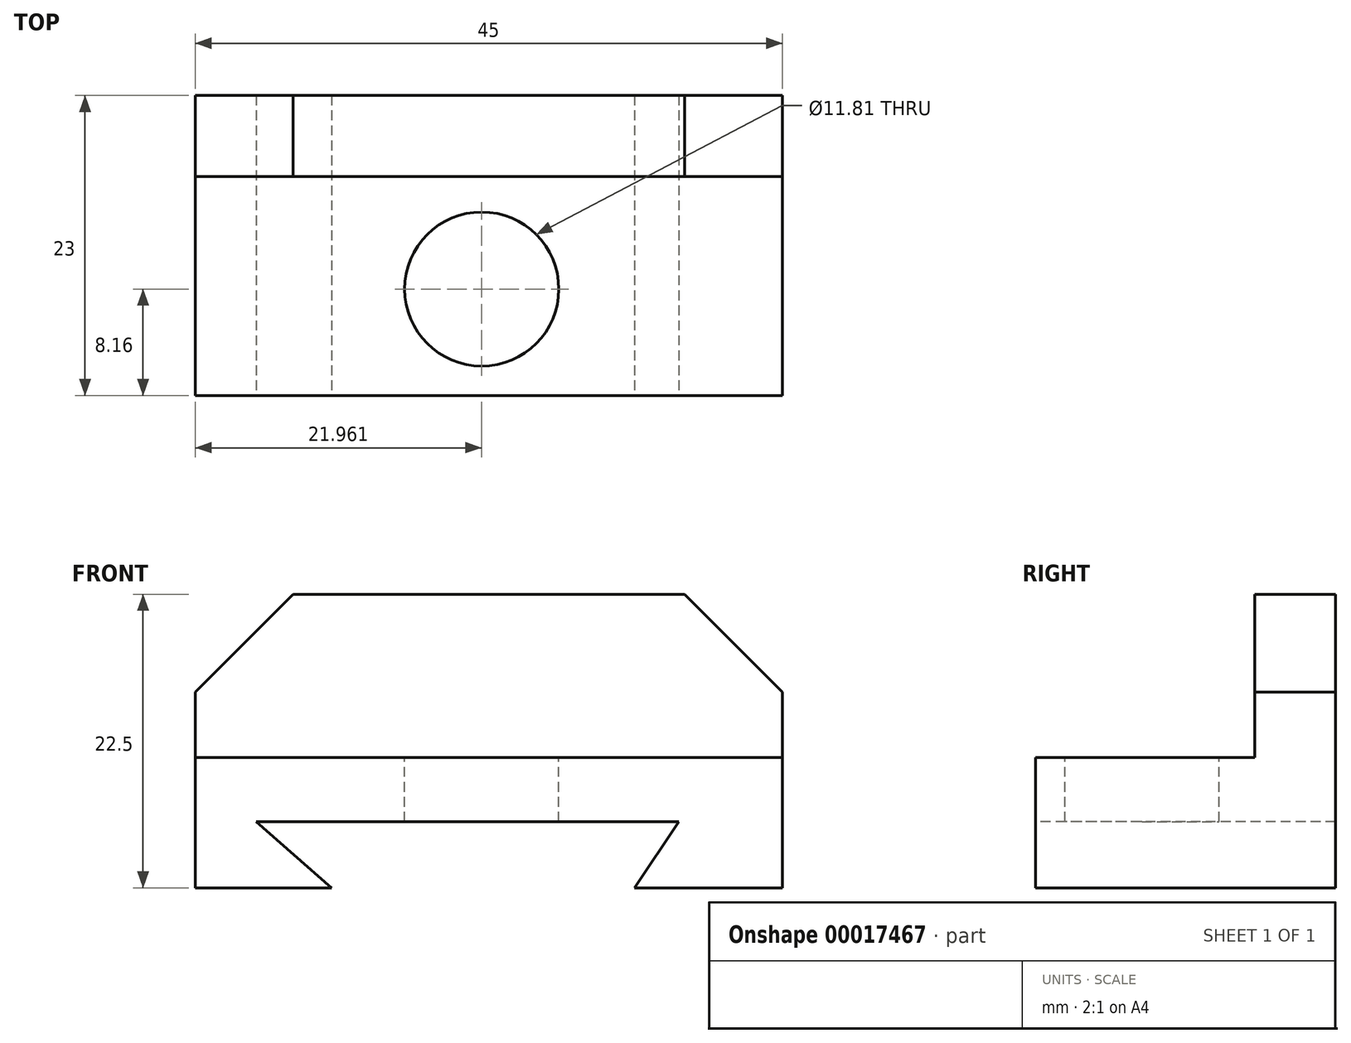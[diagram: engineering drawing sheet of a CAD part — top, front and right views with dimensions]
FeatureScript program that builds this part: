
annotation { "Feature Type Name" : "Feature", "Feature Type Description" : "" }
export const myFeature = defineFeature(function(context is Context, id is Id, definition is map)
    precondition{}
    {
        {
            var Q0;
            Q0=qCreatedBy(makeId("Front.planeOp"),FACE);
            var sketch = newSketch(context, id + "F0", { "sketchPlane" : qUnion([Q0])});
            skLineSegment(sketch, "E0", {"start": v(0, 0) * mm, "end": v(0, 15) * mm});
            skLineSegment(sketch, "E1", {"start": v(0, 15) * mm, "end": v(-7.5, 22.5) * mm});
            skLineSegment(sketch, "E2", {"start": v(-7.5, 22.5) * mm, "end": v(-37.5, 22.5) * mm});
            skLineSegment(sketch, "E3", {"start": v(-37.5, 22.5) * mm, "end": v(-45, 15) * mm});
            skLineSegment(sketch, "E4", {"start": v(-45, 15) * mm, "end": v(-45, 0) * mm});
            skLineSegment(sketch, "E5", {"start": v(-45, 0) * mm, "end": v(0, 0) * mm});
            skLineSegment(sketch, "E6", {"start": v(-45, 15) * mm, "end": v(-45, 10) * mm});
            skLineSegment(sketch, "E7", {"start": v(-45, 10) * mm, "end": v(0, 10) * mm});
            skSolve(sketch);
        }
        {
            var Q0;
            {var subQ1=sQuery(id+"F0.wireOp",EDGE,"E1");Q0=makeQuery(id+"F0.imprint","IMPRINT",FACE,{"disambiguationData":[TD([[makeQuery(id+"F0.imprint","IMPRINT",EDGE,{"derivedFrom":subQ1}),1.0]])]});}
            var Q1;
            Q1=makeQuery(id+"F0.imprint","IMPRINT",FACE,{"disambiguationData":[TD([[makeQuery(id+"F0.imprint","IMPRINT",EDGE,{"derivedFrom":sQuery(id+"F0.wireOp",EDGE,"E4")}),1.0]])]});
            extrude(context, id + "F1", {"entities" : qUnion([Q0, Q1]), "oppositeDirection" : true, "depth" : 6.2 * mm});
        }
        {
            var Q0;
            Q0=makeQuery(id+"F0.imprint","IMPRINT",FACE,{"disambiguationData":[TD([[makeQuery(id+"F0.imprint","IMPRINT",EDGE,{"derivedFrom":sQuery(id+"F0.wireOp",EDGE,"E4")}),1.0]])]});
            extrude(context, id + "F2", {"entities" : qUnion([Q0]), "operationType" : NewBodyOperationType.ADD, "depth" : 16.8 * mm});
        }
        {
            var Q0;
            Q0=makeQuery(id+"F2.opExtrude","SWEPT_FACE",FACE,{"disambiguationData":[OSD([sQuery(id+"F0.wireOp",EDGE,"E7")])]});
            var sketch = newSketch(context, id + "F3", { "sketchPlane" : qUnion([Q0])});
            skCircle(sketch, "E8", {"center": v(-23.04, -8.64) * mm, "radius": 5.9 * mm});
            skSolve(sketch);
        }
        {
            var Q0;
            Q0=makeQuery(id+"F3.imprint","IMPRINT",FACE,{"disambiguationData":[TD([[makeQuery(id+"F3.imprint","IMPRINT",EDGE,{"derivedFrom":sQuery(id+"F3.wireOp",EDGE,"E8")}),1.0]])]});
            extrude(context, id + "F4", {"entities" : qUnion([Q0]), "operationType" : NewBodyOperationType.REMOVE, "endBound" : BoundingType.THROUGH_ALL, "oppositeDirection" : true, "depth" : 25 * mm});
        }
        {
            var Q0;
            Q0=makeQuery(id+"F2.opExtrude","CAP_FACE",FACE,{"disambiguationData":[OSD([sQuery(id+"F0.wireOp",EDGE,"E0"),sQuery(id+"F0.wireOp",EDGE,"E4"),sQuery(id+"F0.wireOp",EDGE,"E5"),sQuery(id+"F0.wireOp",EDGE,"E7")])],"isStart":false});
            var sketch = newSketch(context, id + "F5", { "sketchPlane" : qUnion([Q0])});
            skLineSegment(sketch, "E9", {"start": v(-40.32, 5.06) * mm, "end": v(-34.56, 0) * mm});
            skLineSegment(sketch, "E10", {"start": v(-34.56, 0) * mm, "end": v(-40.32, 5.06) * mm});
            skLineSegment(sketch, "E11", {"start": v(-40.32, 5.06) * mm, "end": v(-7.94, 5.06) * mm});
            skLineSegment(sketch, "E12", {"start": v(-7.94, 5.06) * mm, "end": v(-11.32, 0) * mm});
            skLineSegment(sketch, "E13", {"start": v(-11.32, 0) * mm, "end": v(-34.56, 0) * mm});
            skSolve(sketch);
        }
        {
            var Q0;
            Q0 = qSketchRegion(id + "F5", true);
            extrude(context, id + "F6", {"entities" : qUnion([Q0]), "operationType" : NewBodyOperationType.REMOVE, "endBound" : BoundingType.THROUGH_ALL, "oppositeDirection" : true, "depth" : 25 * mm});
        }
    });
